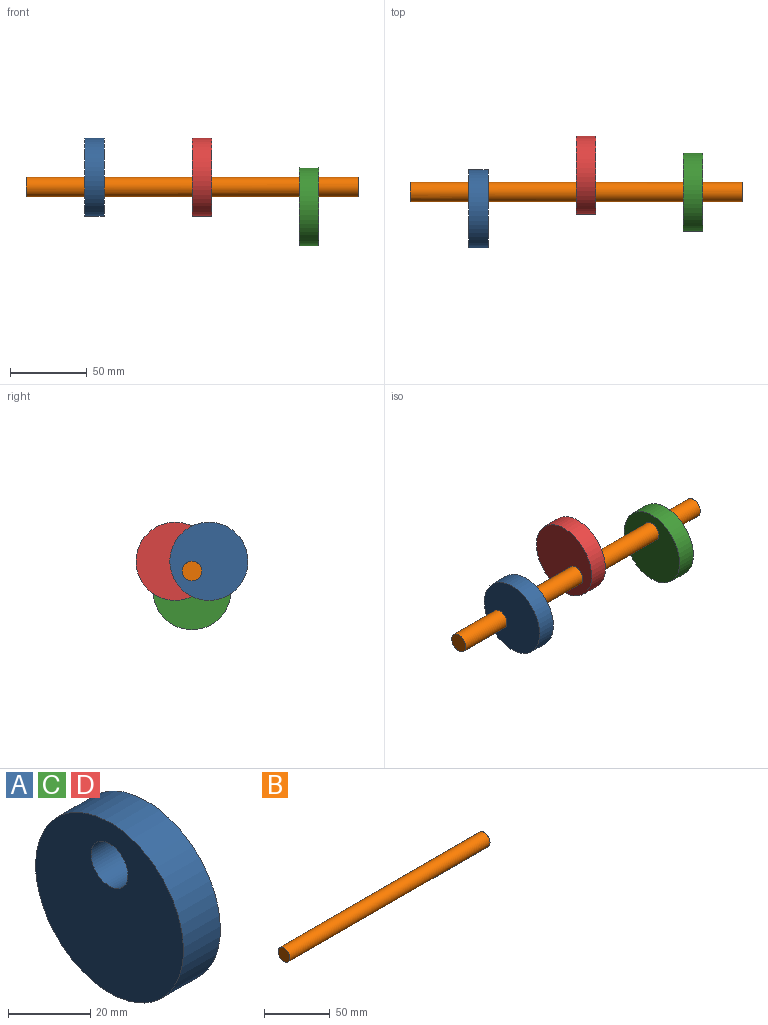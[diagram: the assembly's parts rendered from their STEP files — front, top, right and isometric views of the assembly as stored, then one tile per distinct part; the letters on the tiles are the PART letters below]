
ASSEMBLY  parts=4 mates=3
PART A: 4 faces, bbox 12.7x50.8x50.8 mm
  f0: plane 50.8x50.8mm, normal (1,0,0), area 1900.2mm2, adj f2,f3
  f1: plane 50.8x50.8mm, normal (-1,0,0), area 1900.2mm2, adj f2,f3
  f2: cylinder r=25.4mm len=50.8mm, axis (1,0,0), area 2026.8mm2, adj f0,f1
  f3: cylinder r=6.35mm len=12.7mm, axis (-1,0,0), area 506.7mm2, adj f0,f1
PART B: 3 faces, bbox 215.9x12.7x12.7 mm
  f0: plane 12.7x12.7mm, normal (1,0,0), area 126.7mm2, adj f2
  f1: plane 12.7x12.7mm, normal (-1,0,0), area 126.7mm2, adj f2
  f2: cylinder r=6.35mm len=215.9mm, axis (1,0,0), area 8614mm2, adj f0,f1
PART C: same geometry as A
PART D: same geometry as A
PLACE A rot(axis=(-1,0,0),120deg) t=(-25.4,-49.49,28.58)mm
PLACE B t=(114.3,0,-57.15)mm
PLACE C t=(114.3,0,-57.15)mm
PLACE D rot(axis=(1,0,0),120deg) t=(44.45,49.49,28.57)mm
MATE fastened B.f2 <-> A.f3  axis (1,0,0) through (44.45,0,0)mm
MATE fastened B.f2 <-> D.f3  axis (1,0,0) through (114.3,0,0)mm
MATE fastened C.f3 <-> B.f2  axis (-1,0,0) through (184.15,0,0)mm
